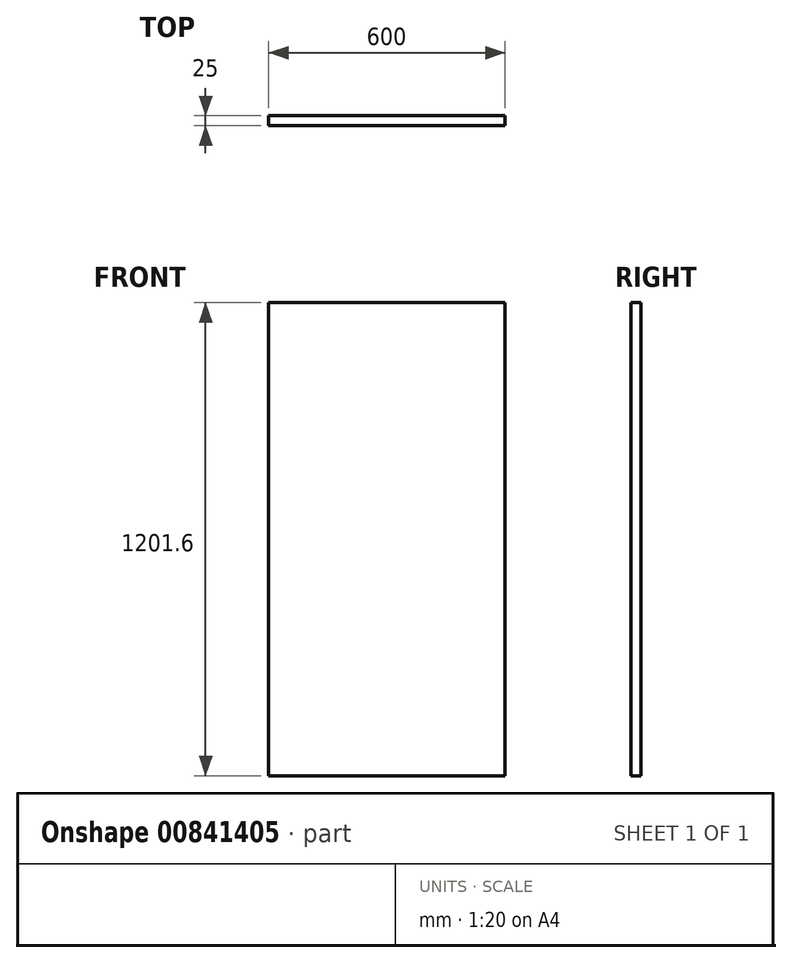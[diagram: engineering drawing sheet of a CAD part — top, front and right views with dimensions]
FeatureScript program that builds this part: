
annotation { "Feature Type Name" : "Feature", "Feature Type Description" : "" }
export const myFeature = defineFeature(function(context is Context, id is Id, definition is map)
    precondition{}
    {
        {
            var Q0;
            Q0=qCreatedBy(makeId("Front.planeOp"),FACE);
            var sketch = newSketch(context, id + "F0", { "sketchPlane" : qUnion([Q0])});
            skLineSegment(sketch, "E0.bottom", {"start": v(300, 600.8) * mm, "end": v(-300, 600.8) * mm});
            skLineSegment(sketch, "E0.top", {"start": v(300, -600.8) * mm, "end": v(-300, -600.8) * mm});
            skLineSegment(sketch, "E0.left", {"start": v(300, 600.8) * mm, "end": v(300, -600.8) * mm});
            skLineSegment(sketch, "E0.right", {"start": v(-300, 600.8) * mm, "end": v(-300, -600.8) * mm});
            skPoint(sketch, "E0.middle", {"position": v(0, 0) * mm});
            skSolve(sketch);
        }
        {
            var Q0;
            Q0 = qSketchRegion(id + "F0", true);
            extrude(context, id + "F1", {"entities" : qUnion([Q0]), "depth" : 25 * mm, "offsetDistance" : 25 * mm});
        }
    });
